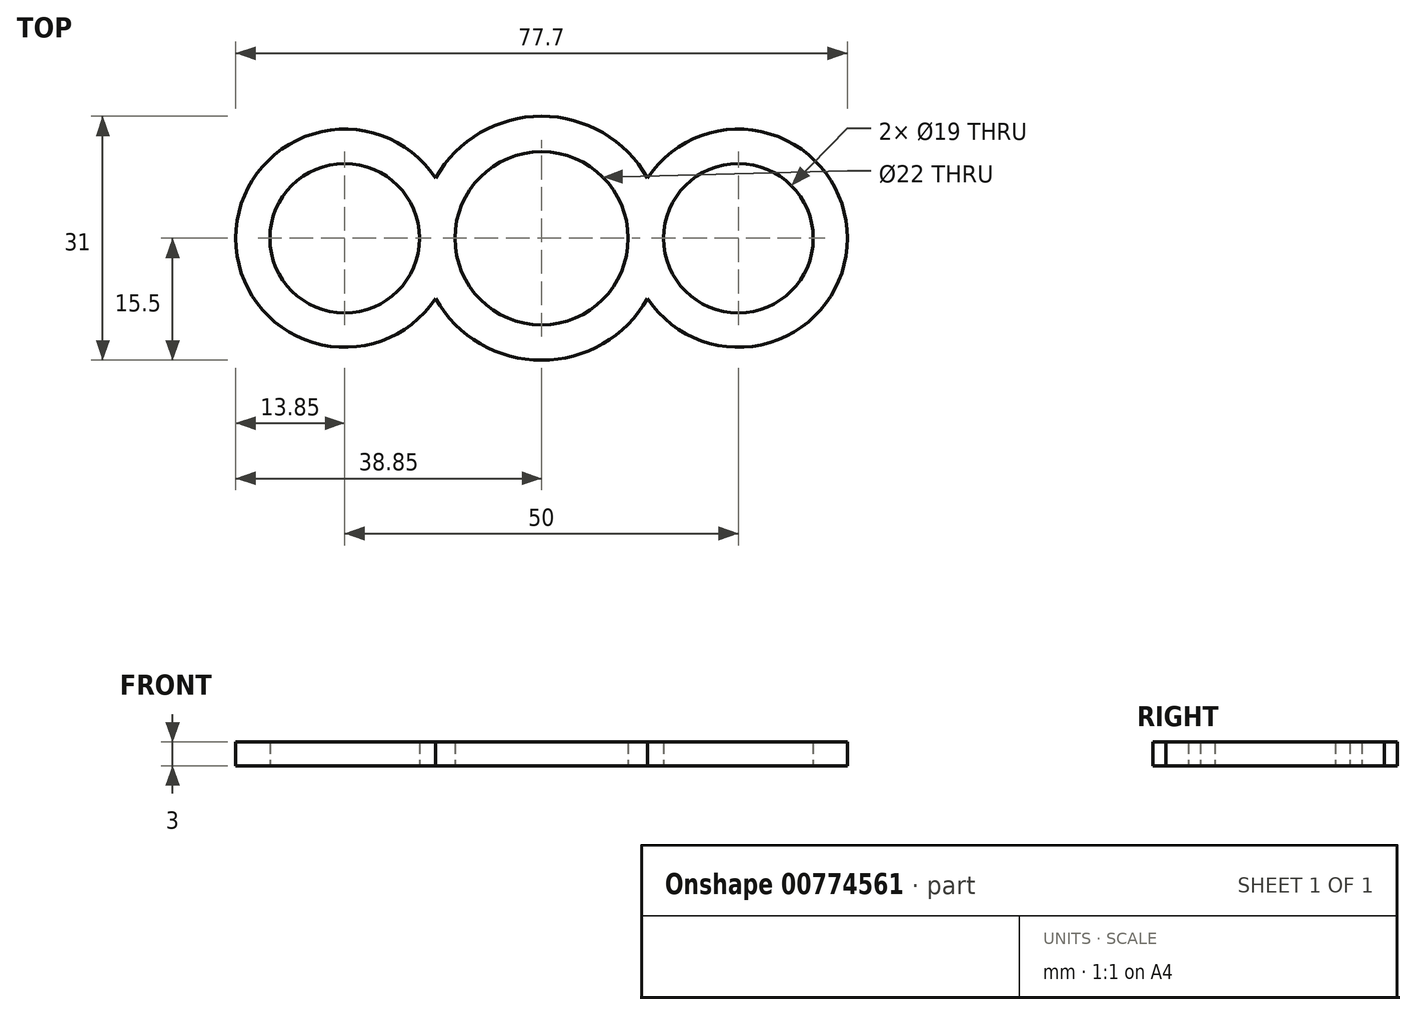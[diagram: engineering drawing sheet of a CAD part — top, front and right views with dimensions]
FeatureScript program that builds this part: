
annotation { "Feature Type Name" : "Feature", "Feature Type Description" : "" }
export const myFeature = defineFeature(function(context is Context, id is Id, definition is map)
    precondition{}
    {
        {
            var Q0;
            Q0=qCreatedBy(makeId("Top.planeOp"),FACE);
            var sketch = newSketch(context, id + "F0", { "sketchPlane" : qUnion([Q0])});
            skCircle(sketch, "E0", {"center": v(0, 0) * mm, "radius": 11 * mm});
            skCircle(sketch, "E1", {"center": v(-25, 0) * mm, "radius": 9.5 * mm});
            skArc(sketch, "E2", {"start": v(-13.47, -7.67) * mm, "mid": v(0, -15.5) * mm, "end": v(13.47, -7.67) * mm});
            skArc(sketch, "E3", {"start": v(-13.47, 7.67) * mm, "mid": v(-38.85, 0) * mm, "end": v(-13.47, -7.67) * mm});
            skCircle(sketch, "E4.MirrorC", {"center": v(25, 0) * mm, "radius": 9.5 * mm});
            skArc(sketch, "E5.MirrorCS", {"start": v(13.47, 7.67) * mm, "mid": v(38.85, 0) * mm, "end": v(13.47, -7.67) * mm});
            skPoint(sketch, "E6", {"position": v(15.5, 0) * mm});
            skArc(sketch, "E7.trimOffspring", {"start": v(13.47, 7.67) * mm, "mid": v(0, 15.5) * mm, "end": v(-13.47, 7.67) * mm});
            skSolve(sketch);
        }
        {
            var Q0;
            Q0 = qSketchRegion(id + "F0", true);
            extrude(context, id + "F1", {"entities" : qUnion([Q0]), "depth" : 3 * mm, "offsetDistance" : 25 * mm});
        }
    });
